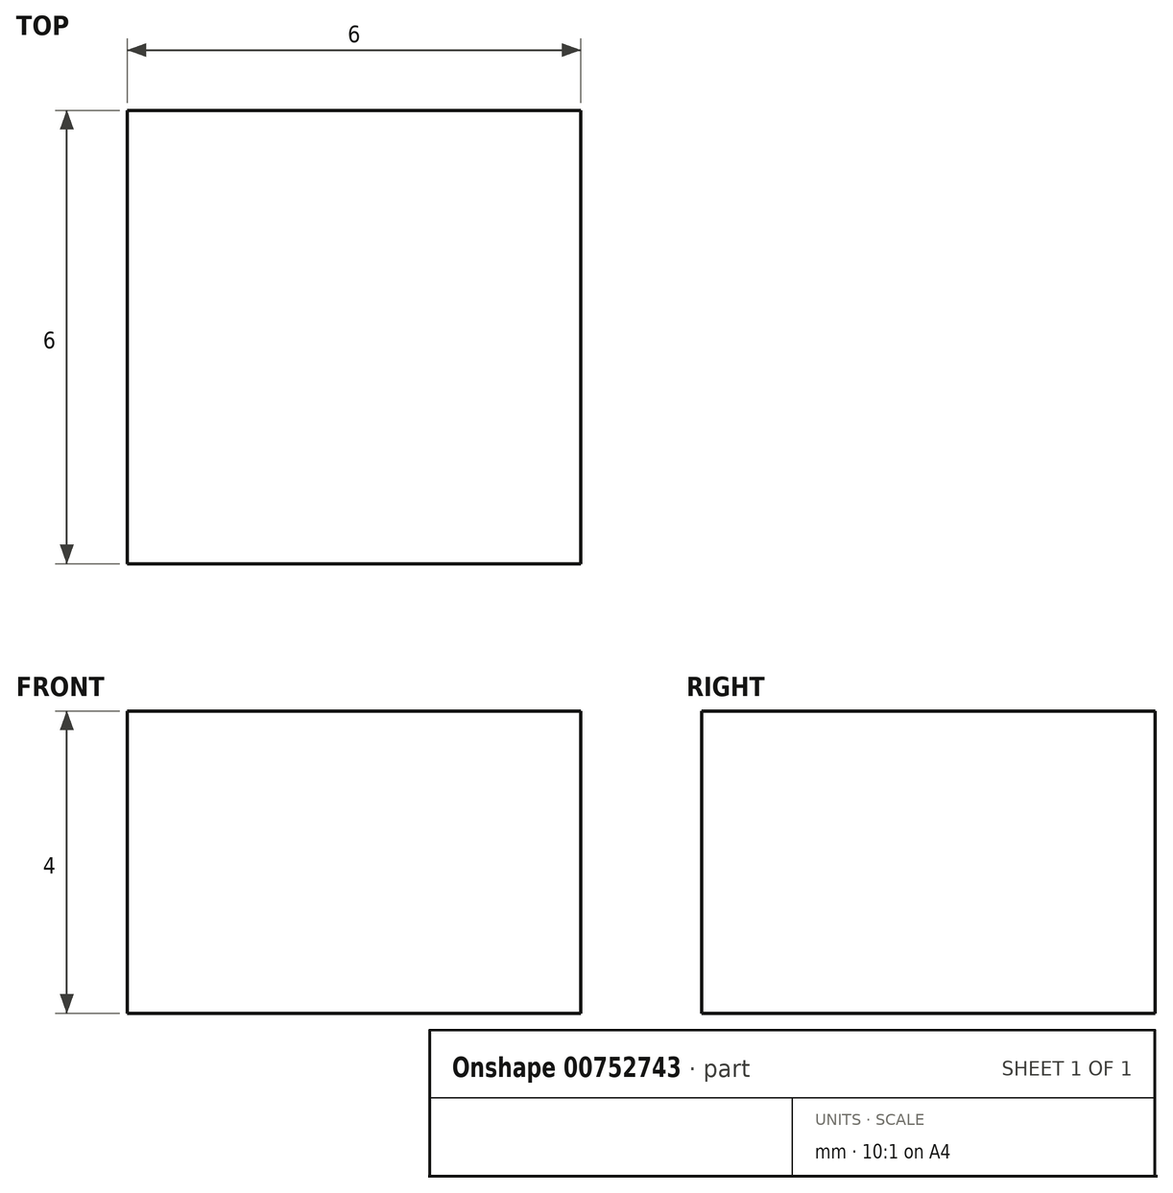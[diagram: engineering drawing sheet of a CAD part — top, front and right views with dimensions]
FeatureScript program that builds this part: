
annotation { "Feature Type Name" : "Feature", "Feature Type Description" : "" }
export const myFeature = defineFeature(function(context is Context, id is Id, definition is map)
    precondition{}
    {
        {
            var Q0;
            Q0=qCreatedBy(makeId("Top.planeOp"),FACE);
            var sketch = newSketch(context, id + "F0", { "sketchPlane" : qUnion([Q0])});
            skLineSegment(sketch, "E0.bottom", {"start": v(0, 0) * mm, "end": v(6, 0) * mm});
            skLineSegment(sketch, "E0.top", {"start": v(0, -6) * mm, "end": v(6, -6) * mm});
            skLineSegment(sketch, "E0.left", {"start": v(0, 0) * mm, "end": v(0, -6) * mm});
            skLineSegment(sketch, "E0.right", {"start": v(6, 0) * mm, "end": v(6, -6) * mm});
            skSolve(sketch);
        }
        {
            var Q0;
            Q0=makeQuery(id+"F0.imprint","IMPRINT",FACE,{"disambiguationData":[TD([[makeQuery(id+"F0.imprint","IMPRINT",EDGE,{"derivedFrom":sQuery(id+"F0.wireOp",EDGE,"E0.bottom")}),-1.0]])]});
            extrude(context, id + "F1", {"entities" : qUnion([Q0]), "depth" : 4 * mm, "offsetDistance" : 25 * mm});
        }
    });
